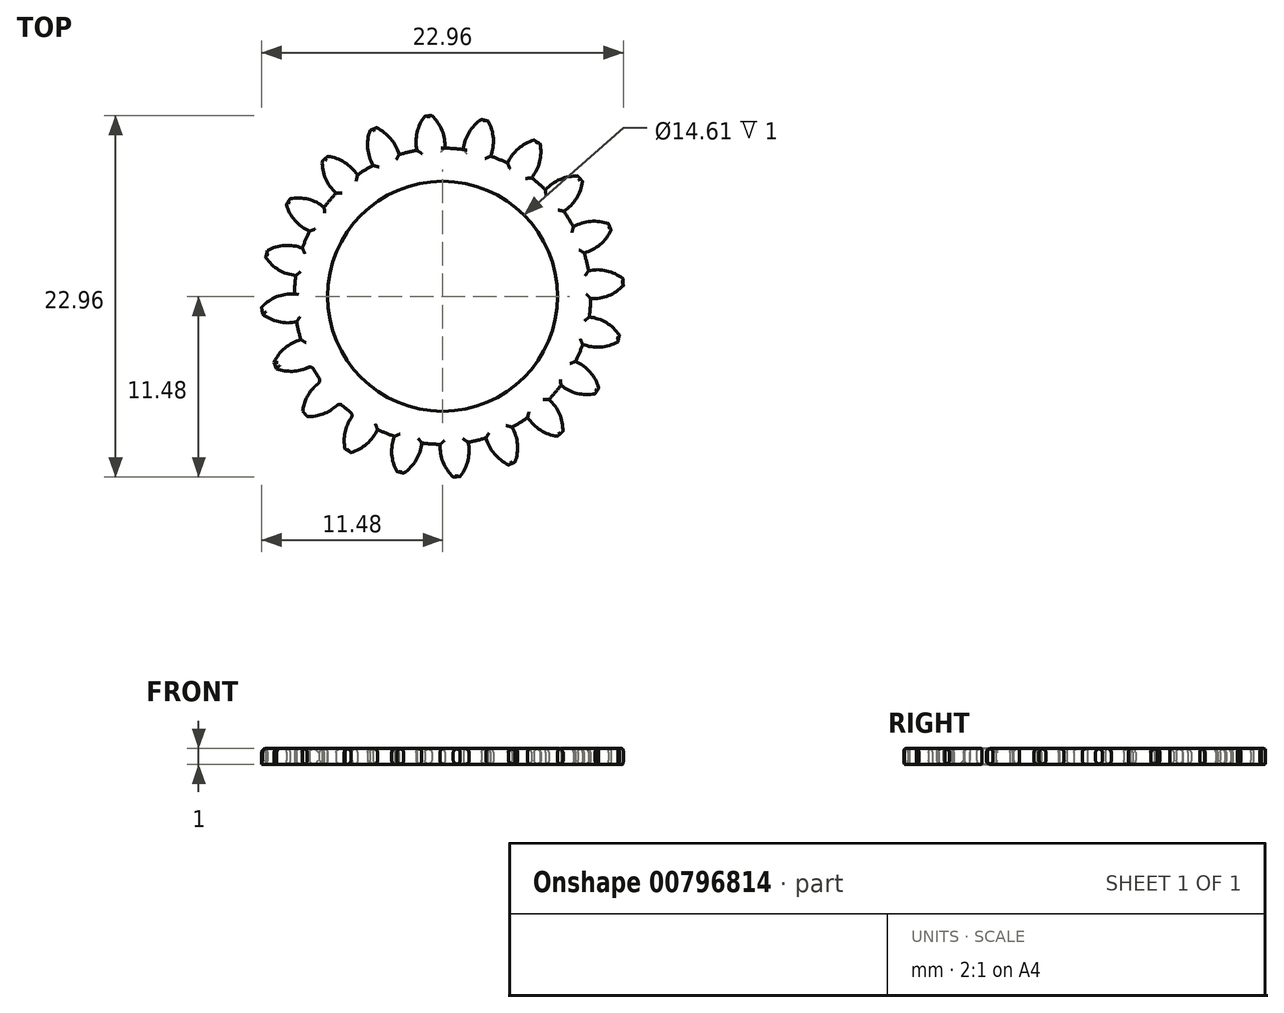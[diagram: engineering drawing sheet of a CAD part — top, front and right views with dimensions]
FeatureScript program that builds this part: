
annotation { "Feature Type Name" : "Feature", "Feature Type Description" : "" }
export const myFeature = defineFeature(function(context is Context, id is Id, definition is map)
    precondition{}
    {
        {
            assignVariable(context, id + "F0", {"name" : "GearDepth", "anyValue" : 1});
        }
        {
            assignVariable(context, id + "F1", {"name" : "TeethFillet", "anyValue" : getVariable(context, 'GearDepth') * .25});
        }
        {
            var Q0;
            Q0=qCreatedBy(makeId("Top.planeOp"),FACE);
            var sketch = newSketch(context, id + "F2", { "sketchPlane" : qUnion([Q0])});
            skCircle(sketch, "E0", {"center": v(0, 0) * mm, "radius": 9.4 * mm});
            skCircle(sketch, "E1", {"center": v(0, 0) * mm, "radius": 10.45 * mm, "construction": true});
            skCircle(sketch, "E2", {"center": v(0, 0) * mm, "radius": 11.5 * mm, "construction": true});
            skLineSegment(sketch, "E3", {"start": v(0, 0) * mm, "end": v(0, 17.6) * mm, "construction": true});
            skLineSegment(sketch, "E4", {"start": v(0, 0) * mm, "end": v(-1.42, 18) * mm, "construction": true});
            skLineSegment(sketch, "E5", {"start": v(0, 10.45) * mm, "end": v(-10.54, 10.45) * mm, "construction": true});
            skLineSegment(sketch, "E6", {"start": v(0, 10.45) * mm, "end": v(-10.3, 6.7) * mm, "construction": true});
            skCircle(sketch, "E7", {"center": v(0, 10.45) * mm, "radius": 2.61 * mm, "construction": true});
            skCircle(sketch, "E8", {"center": v(-2.46, 9.56) * mm, "radius": 2.61 * mm, "construction": true});
            skArc(sketch, "E9", {"start": v(-4.91, 10.45) * mm, "mid": v(-4.92, 10.42) * mm, "end": v(-4.94, 10.39) * mm});
            skArc(sketch, "E10.trimOffspring", {"start": v(0.15, 9.4) * mm, "mid": v(-0.03, 10.54) * mm, "end": v(-0.68, 11.48) * mm});
            skArc(sketch, "E11.MirrorCS", {"start": v(-1.62, 9.27) * mm, "mid": v(-1.62, 10.41) * mm, "end": v(-1.12, 11.45) * mm});
            skLineSegment(sketch, "E12", {"start": v(-1.12, 11.45) * mm, "end": v(-0.68, 11.48) * mm});
            skArc(sketch, "E13.1.0", {"start": v(-2.76, 9) * mm, "mid": v(-3.29, 10.01) * mm, "end": v(-4.2, 10.7) * mm});
            skLineSegment(sketch, "E13.1.1", {"start": v(-4.6, 10.54) * mm, "end": v(-4.2, 10.7) * mm});
            skArc(sketch, "E13.1.2", {"start": v(-4.4, 8.31) * mm, "mid": v(-4.76, 9.4) * mm, "end": v(-4.6, 10.54) * mm});
            skArc(sketch, "E13.2.0", {"start": v(-5.4, 7.7) * mm, "mid": v(-6.22, 8.5) * mm, "end": v(-7.3, 8.89) * mm});
            skLineSegment(sketch, "E13.2.1", {"start": v(-7.64, 8.6) * mm, "end": v(-7.3, 8.89) * mm});
            skArc(sketch, "E13.2.2", {"start": v(-6.76, 6.54) * mm, "mid": v(-7.43, 7.47) * mm, "end": v(-7.64, 8.6) * mm});
            skArc(sketch, "E13.3.0", {"start": v(-7.52, 5.65) * mm, "mid": v(-8.54, 6.17) * mm, "end": v(-9.69, 6.2) * mm});
            skLineSegment(sketch, "E13.3.1", {"start": v(-9.92, 5.82) * mm, "end": v(-9.69, 6.2) * mm});
            skArc(sketch, "E13.3.2", {"start": v(-8.45, 4.13) * mm, "mid": v(-9.37, 4.81) * mm, "end": v(-9.92, 5.82) * mm});
            skArc(sketch, "E13.4.0", {"start": v(-8.9, 3.05) * mm, "mid": v(-10.03, 3.23) * mm, "end": v(-11.13, 2.9) * mm});
            skLineSegment(sketch, "E13.4.1", {"start": v(-11.23, 2.47) * mm, "end": v(-11.13, 2.9) * mm});
            skArc(sketch, "E13.4.2", {"start": v(-9.32, 1.32) * mm, "mid": v(-10.4, 1.68) * mm, "end": v(-11.23, 2.47) * mm});
            skArc(sketch, "E13.5.0", {"start": v(-9.4, 0.15) * mm, "mid": v(-10.54, -0.03) * mm, "end": v(-11.48, -0.68) * mm});
            skLineSegment(sketch, "E13.5.1", {"start": v(-11.45, -1.12) * mm, "end": v(-11.48, -0.68) * mm});
            skArc(sketch, "E13.5.2", {"start": v(-9.27, -1.62) * mm, "mid": v(-10.41, -1.62) * mm, "end": v(-11.45, -1.12) * mm});
            skArc(sketch, "E13.6.0", {"start": v(-9, -2.76) * mm, "mid": v(-10.01, -3.29) * mm, "end": v(-10.7, -4.2) * mm});
            skLineSegment(sketch, "E13.6.1", {"start": v(-10.54, -4.6) * mm, "end": v(-10.7, -4.2) * mm});
            skArc(sketch, "E13.6.2", {"start": v(-8.31, -4.4) * mm, "mid": v(-9.4, -4.76) * mm, "end": v(-10.54, -4.6) * mm});
            skArc(sketch, "E13.7.0", {"start": v(-7.7, -5.4) * mm, "mid": v(-8.5, -6.22) * mm, "end": v(-8.89, -7.3) * mm});
            skLineSegment(sketch, "E13.7.1", {"start": v(-8.6, -7.64) * mm, "end": v(-8.89, -7.3) * mm});
            skArc(sketch, "E13.7.2", {"start": v(-6.54, -6.76) * mm, "mid": v(-7.47, -7.43) * mm, "end": v(-8.6, -7.64) * mm});
            skArc(sketch, "E13.8.0", {"start": v(-5.65, -7.52) * mm, "mid": v(-6.17, -8.54) * mm, "end": v(-6.2, -9.69) * mm});
            skLineSegment(sketch, "E13.8.1", {"start": v(-5.82, -9.92) * mm, "end": v(-6.2, -9.69) * mm});
            skArc(sketch, "E13.8.2", {"start": v(-4.13, -8.45) * mm, "mid": v(-4.81, -9.37) * mm, "end": v(-5.82, -9.92) * mm});
            skArc(sketch, "E13.9.0", {"start": v(-3.05, -8.9) * mm, "mid": v(-3.23, -10.03) * mm, "end": v(-2.9, -11.13) * mm});
            skLineSegment(sketch, "E13.9.1", {"start": v(-2.47, -11.23) * mm, "end": v(-2.9, -11.13) * mm});
            skArc(sketch, "E13.9.2", {"start": v(-1.32, -9.32) * mm, "mid": v(-1.68, -10.4) * mm, "end": v(-2.47, -11.23) * mm});
            skArc(sketch, "E13.10.0", {"start": v(-0.15, -9.4) * mm, "mid": v(0.03, -10.54) * mm, "end": v(0.68, -11.48) * mm});
            skLineSegment(sketch, "E13.10.1", {"start": v(1.12, -11.45) * mm, "end": v(0.68, -11.48) * mm});
            skArc(sketch, "E13.10.2", {"start": v(1.62, -9.27) * mm, "mid": v(1.62, -10.41) * mm, "end": v(1.12, -11.45) * mm});
            skArc(sketch, "E13.11.0", {"start": v(2.76, -9) * mm, "mid": v(3.29, -10.01) * mm, "end": v(4.2, -10.7) * mm});
            skLineSegment(sketch, "E13.11.1", {"start": v(4.6, -10.54) * mm, "end": v(4.2, -10.7) * mm});
            skArc(sketch, "E13.11.2", {"start": v(4.4, -8.31) * mm, "mid": v(4.76, -9.4) * mm, "end": v(4.6, -10.54) * mm});
            skArc(sketch, "E13.12.0", {"start": v(5.4, -7.7) * mm, "mid": v(6.22, -8.5) * mm, "end": v(7.3, -8.89) * mm});
            skLineSegment(sketch, "E13.12.1", {"start": v(7.64, -8.6) * mm, "end": v(7.3, -8.89) * mm});
            skArc(sketch, "E13.12.2", {"start": v(6.76, -6.54) * mm, "mid": v(7.43, -7.47) * mm, "end": v(7.64, -8.6) * mm});
            skArc(sketch, "E13.13.0", {"start": v(7.52, -5.65) * mm, "mid": v(8.54, -6.17) * mm, "end": v(9.69, -6.2) * mm});
            skLineSegment(sketch, "E13.13.1", {"start": v(9.92, -5.82) * mm, "end": v(9.69, -6.2) * mm});
            skArc(sketch, "E13.13.2", {"start": v(8.45, -4.13) * mm, "mid": v(9.37, -4.81) * mm, "end": v(9.92, -5.82) * mm});
            skArc(sketch, "E13.14.0", {"start": v(8.9, -3.05) * mm, "mid": v(10.03, -3.23) * mm, "end": v(11.13, -2.9) * mm});
            skLineSegment(sketch, "E13.14.1", {"start": v(11.23, -2.47) * mm, "end": v(11.13, -2.9) * mm});
            skArc(sketch, "E13.14.2", {"start": v(9.32, -1.32) * mm, "mid": v(10.4, -1.68) * mm, "end": v(11.23, -2.47) * mm});
            skArc(sketch, "E13.15.0", {"start": v(9.4, -0.15) * mm, "mid": v(10.54, 0.03) * mm, "end": v(11.48, 0.68) * mm});
            skLineSegment(sketch, "E13.15.1", {"start": v(11.45, 1.12) * mm, "end": v(11.48, 0.68) * mm});
            skArc(sketch, "E13.15.2", {"start": v(9.27, 1.62) * mm, "mid": v(10.41, 1.62) * mm, "end": v(11.45, 1.12) * mm});
            skArc(sketch, "E13.16.0", {"start": v(9, 2.76) * mm, "mid": v(10.01, 3.29) * mm, "end": v(10.7, 4.2) * mm});
            skLineSegment(sketch, "E13.16.1", {"start": v(10.54, 4.6) * mm, "end": v(10.7, 4.2) * mm});
            skArc(sketch, "E13.16.2", {"start": v(8.31, 4.4) * mm, "mid": v(9.4, 4.76) * mm, "end": v(10.54, 4.6) * mm});
            skArc(sketch, "E13.17.0", {"start": v(7.7, 5.4) * mm, "mid": v(8.5, 6.22) * mm, "end": v(8.89, 7.3) * mm});
            skLineSegment(sketch, "E13.17.1", {"start": v(8.6, 7.64) * mm, "end": v(8.89, 7.3) * mm});
            skArc(sketch, "E13.17.2", {"start": v(6.54, 6.76) * mm, "mid": v(7.47, 7.43) * mm, "end": v(8.6, 7.64) * mm});
            skArc(sketch, "E13.18.0", {"start": v(5.65, 7.52) * mm, "mid": v(6.17, 8.54) * mm, "end": v(6.2, 9.69) * mm});
            skLineSegment(sketch, "E13.18.1", {"start": v(5.82, 9.92) * mm, "end": v(6.2, 9.69) * mm});
            skArc(sketch, "E13.18.2", {"start": v(4.13, 8.45) * mm, "mid": v(4.81, 9.37) * mm, "end": v(5.82, 9.92) * mm});
            skArc(sketch, "E13.19.0", {"start": v(3.05, 8.9) * mm, "mid": v(3.23, 10.03) * mm, "end": v(2.9, 11.13) * mm});
            skLineSegment(sketch, "E13.19.1", {"start": v(2.47, 11.23) * mm, "end": v(2.9, 11.13) * mm});
            skArc(sketch, "E13.19.2", {"start": v(1.32, 9.32) * mm, "mid": v(1.68, 10.4) * mm, "end": v(2.47, 11.23) * mm});
            skCircle(sketch, "E14", {"center": v(0, 0) * mm, "radius": 2.5 * mm});
            skSolve(sketch);
        }
        {
            var Q0;
            {var subQ0=sQuery(id+"F2.wireOp",EDGE,"E10.trimOffspring");Q0=makeQuery(id+"F2.imprint","IMPRINT",FACE,{"disambiguationData":[TD([[makeQuery(id+"F2.imprint","IMPRINT",EDGE,{"derivedFrom":subQ0}),1.0]])]});}
            var Q1;
            {var subQ0=sQuery(id+"F2.wireOp",EDGE,"E0");var subQ1=makeQuery(id+"F2.imprint","INTERSECT",VERTEX,{"derivedFrom":[subQ0,sQuery(id+"F2.wireOp",EDGE,"E10.trimOffspring")]});Q1=makeQuery(id+"F2.imprint","IMPRINT",FACE,{"disambiguationData":[TD([[makeQuery(id+"F2.imprint","IMPRINT",EDGE,{"disambiguationData":[TD([[subQ1,-1.0]])],"derivedFrom":subQ0}),1.0]])]});}
            var Q2;
            {var subQ0=sQuery(id+"F2.wireOp",EDGE,"E13.1.0");Q2=makeQuery(id+"F2.imprint","IMPRINT",FACE,{"disambiguationData":[TD([[makeQuery(id+"F2.imprint","IMPRINT",EDGE,{"derivedFrom":subQ0}),1.0]])]});}
            var Q3;
            {var subQ0=sQuery(id+"F2.wireOp",EDGE,"E13.2.0");Q3=makeQuery(id+"F2.imprint","IMPRINT",FACE,{"disambiguationData":[TD([[makeQuery(id+"F2.imprint","IMPRINT",EDGE,{"derivedFrom":subQ0}),1.0]])]});}
            var Q4;
            {var subQ0=sQuery(id+"F2.wireOp",EDGE,"E13.3.0");Q4=makeQuery(id+"F2.imprint","IMPRINT",FACE,{"disambiguationData":[TD([[makeQuery(id+"F2.imprint","IMPRINT",EDGE,{"derivedFrom":subQ0}),1.0]])]});}
            var Q5;
            {var subQ0=sQuery(id+"F2.wireOp",EDGE,"E13.4.0");Q5=makeQuery(id+"F2.imprint","IMPRINT",FACE,{"disambiguationData":[TD([[makeQuery(id+"F2.imprint","IMPRINT",EDGE,{"derivedFrom":subQ0}),1.0]])]});}
            var Q6;
            {var subQ0=sQuery(id+"F2.wireOp",EDGE,"E13.5.0");Q6=makeQuery(id+"F2.imprint","IMPRINT",FACE,{"disambiguationData":[TD([[makeQuery(id+"F2.imprint","IMPRINT",EDGE,{"derivedFrom":subQ0}),1.0]])]});}
            var Q7;
            {var subQ0=sQuery(id+"F2.wireOp",EDGE,"E13.6.0");Q7=makeQuery(id+"F2.imprint","IMPRINT",FACE,{"disambiguationData":[TD([[makeQuery(id+"F2.imprint","IMPRINT",EDGE,{"derivedFrom":subQ0}),1.0]])]});}
            var Q8;
            {var subQ0=sQuery(id+"F2.wireOp",EDGE,"E13.7.0");Q8=makeQuery(id+"F2.imprint","IMPRINT",FACE,{"disambiguationData":[TD([[makeQuery(id+"F2.imprint","IMPRINT",EDGE,{"derivedFrom":subQ0}),1.0]])]});}
            var Q9;
            {var subQ0=sQuery(id+"F2.wireOp",EDGE,"E13.8.0");Q9=makeQuery(id+"F2.imprint","IMPRINT",FACE,{"disambiguationData":[TD([[makeQuery(id+"F2.imprint","IMPRINT",EDGE,{"derivedFrom":subQ0}),1.0]])]});}
            var Q10;
            {var subQ0=sQuery(id+"F2.wireOp",EDGE,"E13.9.0");Q10=makeQuery(id+"F2.imprint","IMPRINT",FACE,{"disambiguationData":[TD([[makeQuery(id+"F2.imprint","IMPRINT",EDGE,{"derivedFrom":subQ0}),1.0]])]});}
            var Q11;
            {var subQ0=sQuery(id+"F2.wireOp",EDGE,"E13.10.0");Q11=makeQuery(id+"F2.imprint","IMPRINT",FACE,{"disambiguationData":[TD([[makeQuery(id+"F2.imprint","IMPRINT",EDGE,{"derivedFrom":subQ0}),1.0]])]});}
            var Q12;
            {var subQ0=sQuery(id+"F2.wireOp",EDGE,"E13.11.0");Q12=makeQuery(id+"F2.imprint","IMPRINT",FACE,{"disambiguationData":[TD([[makeQuery(id+"F2.imprint","IMPRINT",EDGE,{"derivedFrom":subQ0}),1.0]])]});}
            var Q13;
            {var subQ0=sQuery(id+"F2.wireOp",EDGE,"E13.12.0");Q13=makeQuery(id+"F2.imprint","IMPRINT",FACE,{"disambiguationData":[TD([[makeQuery(id+"F2.imprint","IMPRINT",EDGE,{"derivedFrom":subQ0}),1.0]])]});}
            var Q14;
            {var subQ0=sQuery(id+"F2.wireOp",EDGE,"E13.13.0");Q14=makeQuery(id+"F2.imprint","IMPRINT",FACE,{"disambiguationData":[TD([[makeQuery(id+"F2.imprint","IMPRINT",EDGE,{"derivedFrom":subQ0}),1.0]])]});}
            var Q15;
            {var subQ0=sQuery(id+"F2.wireOp",EDGE,"E13.14.0");Q15=makeQuery(id+"F2.imprint","IMPRINT",FACE,{"disambiguationData":[TD([[makeQuery(id+"F2.imprint","IMPRINT",EDGE,{"derivedFrom":subQ0}),1.0]])]});}
            var Q16;
            {var subQ0=sQuery(id+"F2.wireOp",EDGE,"E13.15.0");Q16=makeQuery(id+"F2.imprint","IMPRINT",FACE,{"disambiguationData":[TD([[makeQuery(id+"F2.imprint","IMPRINT",EDGE,{"derivedFrom":subQ0}),1.0]])]});}
            var Q17;
            {var subQ0=sQuery(id+"F2.wireOp",EDGE,"E13.16.0");Q17=makeQuery(id+"F2.imprint","IMPRINT",FACE,{"disambiguationData":[TD([[makeQuery(id+"F2.imprint","IMPRINT",EDGE,{"derivedFrom":subQ0}),1.0]])]});}
            var Q18;
            {var subQ0=sQuery(id+"F2.wireOp",EDGE,"E13.17.0");Q18=makeQuery(id+"F2.imprint","IMPRINT",FACE,{"disambiguationData":[TD([[makeQuery(id+"F2.imprint","IMPRINT",EDGE,{"derivedFrom":subQ0}),1.0]])]});}
            var Q19;
            {var subQ0=sQuery(id+"F2.wireOp",EDGE,"E13.18.0");Q19=makeQuery(id+"F2.imprint","IMPRINT",FACE,{"disambiguationData":[TD([[makeQuery(id+"F2.imprint","IMPRINT",EDGE,{"derivedFrom":subQ0}),1.0]])]});}
            var Q20;
            {var subQ0=sQuery(id+"F2.wireOp",EDGE,"E13.19.0");Q20=makeQuery(id+"F2.imprint","IMPRINT",FACE,{"disambiguationData":[TD([[makeQuery(id+"F2.imprint","IMPRINT",EDGE,{"derivedFrom":subQ0}),1.0]])]});}
            var Q21;
            Q21=sQuery(id+"F2.wireOp",EDGE,"E0");
            var Q22;
            Q22=sQuery(id+"F2.wireOp",EDGE,"E10.trimOffspring");
            var Q23;
            Q23=sQuery(id+"F2.wireOp",EDGE,"E12");
            var Q24;
            Q24=sQuery(id+"F2.wireOp",EDGE,"E11.MirrorCS");
            extrude(context, id + "F3", {"entities" : qUnion([Q0, Q1, Q2, Q3, Q4, Q5, Q6, Q7, Q8, Q9, Q10, Q11, Q12, Q13, Q14, Q15, Q16, Q17, Q18, Q19, Q20]), "surfaceEntities" : qUnion([Q21, Q22, Q23, Q24]), "depth" : (getVariable(context, 'GearDepth')) * mm});
        }
        {
            var Q0;
            Q0=makeQuery(id+"F3.opExtrude","CAP_EDGE",EDGE,{"disambiguationData":[OSD([sQuery(id+"F2.wireOp",EDGE,"E13.5.2")])],"isStart":false});
            var Q1;
            Q1=makeQuery(id+"F3.opExtrude","CAP_EDGE",EDGE,{"disambiguationData":[OSD([sQuery(id+"F2.wireOp",EDGE,"E13.5.1")])],"isStart":false});
            var Q2;
            {var subQ0=sQuery(id+"F2.wireOp",EDGE,"E0");Q2=makeQuery(id+"F3.opExtrude","CAP_EDGE",EDGE,{"disambiguationData":[OSD([subQ0]),TDD([makeQuery(id+"F2.imprint","IMPRINT",EDGE,{"disambiguationData":[TD([[makeQuery(id+"F2.imprint","INTERSECT",VERTEX,{"derivedFrom":[subQ0,sQuery(id+"F2.wireOp",EDGE,"E13.5.2")]}),-1.0]])],"derivedFrom":subQ0})])],"isStart":false});}
            var Q3;
            Q3=makeQuery(id+"F3.opExtrude","CAP_EDGE",EDGE,{"disambiguationData":[OSD([sQuery(id+"F2.wireOp",EDGE,"E13.6.0")])],"isStart":false});
            var Q4;
            Q4=makeQuery(id+"F3.opExtrude","CAP_EDGE",EDGE,{"disambiguationData":[OSD([sQuery(id+"F2.wireOp",EDGE,"E13.6.1")])],"isStart":false});
            var Q5;
            Q5=makeQuery(id+"F3.opExtrude","CAP_EDGE",EDGE,{"disambiguationData":[OSD([sQuery(id+"F2.wireOp",EDGE,"E13.6.2")])],"isStart":false});
            var Q6;
            {var subQ0=sQuery(id+"F2.wireOp",EDGE,"E0");Q6=makeQuery(id+"F3.opExtrude","SWEPT_FACE",FACE,{"disambiguationData":[OSD([subQ0]),TDD([makeQuery(id+"F2.imprint","IMPRINT",EDGE,{"disambiguationData":[TD([[makeQuery(id+"F2.imprint","INTERSECT",VERTEX,{"derivedFrom":[subQ0,sQuery(id+"F2.wireOp",EDGE,"E13.6.2")]}),-1.0]])],"derivedFrom":subQ0})])]});}
            var Q7;
            {var subQ0=sQuery(id+"F2.wireOp",EDGE,"E0");Q7=makeQuery(id+"F3.opExtrude","CAP_EDGE",EDGE,{"disambiguationData":[OSD([subQ0]),TDD([makeQuery(id+"F2.imprint","IMPRINT",EDGE,{"disambiguationData":[TD([[makeQuery(id+"F2.imprint","INTERSECT",VERTEX,{"derivedFrom":[subQ0,sQuery(id+"F2.wireOp",EDGE,"E13.6.2")]}),-1.0]])],"derivedFrom":subQ0})])],"isStart":false});}
            var Q8;
            Q8=makeQuery(id+"F3.opExtrude","CAP_EDGE",EDGE,{"disambiguationData":[OSD([sQuery(id+"F2.wireOp",EDGE,"E13.7.2")])],"isStart":true});
            var Q9;
            {var subQ0=sQuery(id+"F2.wireOp",EDGE,"E0");Q9=makeQuery(id+"F3.opExtrude","CAP_EDGE",EDGE,{"disambiguationData":[OSD([subQ0]),TDD([makeQuery(id+"F2.imprint","IMPRINT",EDGE,{"disambiguationData":[TD([[makeQuery(id+"F2.imprint","INTERSECT",VERTEX,{"derivedFrom":[subQ0,sQuery(id+"F2.wireOp",EDGE,"E13.7.2")]}),-1.0]])],"derivedFrom":subQ0})])],"isStart":true});}
            var Q10;
            Q10=makeQuery(id+"F3.opExtrude","CAP_EDGE",EDGE,{"disambiguationData":[OSD([sQuery(id+"F2.wireOp",EDGE,"E13.7.2")])],"isStart":false});
            var Q11;
            {var subQ0=sQuery(id+"F2.wireOp",EDGE,"E0");Q11=makeQuery(id+"F3.opExtrude","CAP_EDGE",EDGE,{"disambiguationData":[OSD([subQ0]),TDD([makeQuery(id+"F2.imprint","IMPRINT",EDGE,{"disambiguationData":[TD([[makeQuery(id+"F2.imprint","INTERSECT",VERTEX,{"derivedFrom":[subQ0,sQuery(id+"F2.wireOp",EDGE,"E13.7.2")]}),-1.0]])],"derivedFrom":subQ0})])],"isStart":false});}
            var Q12;
            Q12=makeQuery(id+"F3.opExtrude","CAP_EDGE",EDGE,{"disambiguationData":[OSD([sQuery(id+"F2.wireOp",EDGE,"E13.8.0")])],"isStart":false});
            var Q13;
            {var subQ0=sQuery(id+"F2.wireOp",EDGE,"E0");Q13=makeQuery(id+"F3.opExtrude","SWEPT_FACE",FACE,{"disambiguationData":[OSD([subQ0]),TDD([makeQuery(id+"F2.imprint","IMPRINT",EDGE,{"disambiguationData":[TD([[makeQuery(id+"F2.imprint","INTERSECT",VERTEX,{"derivedFrom":[subQ0,sQuery(id+"F2.wireOp",EDGE,"E13.7.2")]}),-1.0]])],"derivedFrom":subQ0})])]});}
            var Q14;
            Q14=makeQuery(id+"F3.opExtrude","CAP_EDGE",EDGE,{"disambiguationData":[OSD([sQuery(id+"F2.wireOp",EDGE,"E13.6.0")])],"isStart":true});
            var Q15;
            Q15=makeQuery(id+"F3.opExtrude","CAP_EDGE",EDGE,{"disambiguationData":[OSD([sQuery(id+"F2.wireOp",EDGE,"E13.8.2")])],"isStart":false});
            var Q16;
            {var subQ0=sQuery(id+"F2.wireOp",EDGE,"E0");Q16=makeQuery(id+"F3.opExtrude","CAP_EDGE",EDGE,{"disambiguationData":[OSD([subQ0]),TDD([makeQuery(id+"F2.imprint","IMPRINT",EDGE,{"disambiguationData":[TD([[makeQuery(id+"F2.imprint","INTERSECT",VERTEX,{"derivedFrom":[subQ0,sQuery(id+"F2.wireOp",EDGE,"E13.8.2")]}),-1.0]])],"derivedFrom":subQ0})])],"isStart":false});}
            var Q17;
            Q17=makeQuery(id+"F3.opExtrude","CAP_EDGE",EDGE,{"disambiguationData":[OSD([sQuery(id+"F2.wireOp",EDGE,"E13.9.0")])],"isStart":false});
            var Q18;
            Q18=makeQuery(id+"F3.opExtrude","CAP_EDGE",EDGE,{"disambiguationData":[OSD([sQuery(id+"F2.wireOp",EDGE,"E13.9.2")])],"isStart":false});
            var Q19;
            {var subQ0=sQuery(id+"F2.wireOp",EDGE,"E0");Q19=makeQuery(id+"F3.opExtrude","CAP_EDGE",EDGE,{"disambiguationData":[OSD([subQ0]),TDD([makeQuery(id+"F2.imprint","IMPRINT",EDGE,{"disambiguationData":[TD([[makeQuery(id+"F2.imprint","INTERSECT",VERTEX,{"derivedFrom":[subQ0,sQuery(id+"F2.wireOp",EDGE,"E13.9.2")]}),-1.0]])],"derivedFrom":subQ0})])],"isStart":false});}
            var Q20;
            Q20=makeQuery(id+"F3.opExtrude","CAP_EDGE",EDGE,{"disambiguationData":[OSD([sQuery(id+"F2.wireOp",EDGE,"E13.10.0")])],"isStart":false});
            var Q21;
            Q21=makeQuery(id+"F3.opExtrude","CAP_EDGE",EDGE,{"disambiguationData":[OSD([sQuery(id+"F2.wireOp",EDGE,"E13.10.2")])],"isStart":false});
            var Q22;
            {var subQ0=sQuery(id+"F2.wireOp",EDGE,"E0");Q22=makeQuery(id+"F3.opExtrude","CAP_EDGE",EDGE,{"disambiguationData":[OSD([subQ0]),TDD([makeQuery(id+"F2.imprint","IMPRINT",EDGE,{"disambiguationData":[TD([[makeQuery(id+"F2.imprint","INTERSECT",VERTEX,{"derivedFrom":[subQ0,sQuery(id+"F2.wireOp",EDGE,"E13.10.2")]}),-1.0]])],"derivedFrom":subQ0})])],"isStart":false});}
            var Q23;
            Q23=makeQuery(id+"F3.opExtrude","CAP_EDGE",EDGE,{"disambiguationData":[OSD([sQuery(id+"F2.wireOp",EDGE,"E13.11.0")])],"isStart":false});
            var Q24;
            Q24=makeQuery(id+"F3.opExtrude","CAP_EDGE",EDGE,{"disambiguationData":[OSD([sQuery(id+"F2.wireOp",EDGE,"E13.11.2")])],"isStart":false});
            var Q25;
            {var subQ0=sQuery(id+"F2.wireOp",EDGE,"E0");Q25=makeQuery(id+"F3.opExtrude","CAP_EDGE",EDGE,{"disambiguationData":[OSD([subQ0]),TDD([makeQuery(id+"F2.imprint","IMPRINT",EDGE,{"disambiguationData":[TD([[makeQuery(id+"F2.imprint","INTERSECT",VERTEX,{"derivedFrom":[subQ0,sQuery(id+"F2.wireOp",EDGE,"E13.11.2")]}),-1.0]])],"derivedFrom":subQ0})])],"isStart":false});}
            var Q26;
            Q26=makeQuery(id+"F3.opExtrude","CAP_EDGE",EDGE,{"disambiguationData":[OSD([sQuery(id+"F2.wireOp",EDGE,"E13.12.0")])],"isStart":false});
            var Q27;
            Q27=makeQuery(id+"F3.opExtrude","CAP_EDGE",EDGE,{"disambiguationData":[OSD([sQuery(id+"F2.wireOp",EDGE,"E13.12.2")])],"isStart":false});
            var Q28;
            {var subQ0=sQuery(id+"F2.wireOp",EDGE,"E0");Q28=makeQuery(id+"F3.opExtrude","CAP_EDGE",EDGE,{"disambiguationData":[OSD([subQ0]),TDD([makeQuery(id+"F2.imprint","IMPRINT",EDGE,{"disambiguationData":[TD([[makeQuery(id+"F2.imprint","INTERSECT",VERTEX,{"derivedFrom":[subQ0,sQuery(id+"F2.wireOp",EDGE,"E13.12.2")]}),-1.0]])],"derivedFrom":subQ0})])],"isStart":false});}
            var Q29;
            Q29=makeQuery(id+"F3.opExtrude","CAP_EDGE",EDGE,{"disambiguationData":[OSD([sQuery(id+"F2.wireOp",EDGE,"E13.13.0")])],"isStart":false});
            var Q30;
            Q30=makeQuery(id+"F3.opExtrude","CAP_EDGE",EDGE,{"disambiguationData":[OSD([sQuery(id+"F2.wireOp",EDGE,"E13.13.2")])],"isStart":false});
            var Q31;
            {var subQ0=sQuery(id+"F2.wireOp",EDGE,"E0");Q31=makeQuery(id+"F3.opExtrude","CAP_EDGE",EDGE,{"disambiguationData":[OSD([subQ0]),TDD([makeQuery(id+"F2.imprint","IMPRINT",EDGE,{"disambiguationData":[TD([[makeQuery(id+"F2.imprint","INTERSECT",VERTEX,{"derivedFrom":[subQ0,sQuery(id+"F2.wireOp",EDGE,"E13.13.2")]}),-1.0]])],"derivedFrom":subQ0})])],"isStart":false});}
            var Q32;
            Q32=makeQuery(id+"F3.opExtrude","CAP_EDGE",EDGE,{"disambiguationData":[OSD([sQuery(id+"F2.wireOp",EDGE,"E13.14.0")])],"isStart":false});
            var Q33;
            Q33=makeQuery(id+"F3.opExtrude","CAP_EDGE",EDGE,{"disambiguationData":[OSD([sQuery(id+"F2.wireOp",EDGE,"E13.14.2")])],"isStart":false});
            var Q34;
            {var subQ0=sQuery(id+"F2.wireOp",EDGE,"E0");Q34=makeQuery(id+"F3.opExtrude","CAP_EDGE",EDGE,{"disambiguationData":[OSD([subQ0]),TDD([makeQuery(id+"F2.imprint","IMPRINT",EDGE,{"disambiguationData":[TD([[makeQuery(id+"F2.imprint","INTERSECT",VERTEX,{"derivedFrom":[subQ0,sQuery(id+"F2.wireOp",EDGE,"E13.14.2")]}),-1.0]])],"derivedFrom":subQ0})])],"isStart":false});}
            var Q35;
            Q35=makeQuery(id+"F3.opExtrude","CAP_EDGE",EDGE,{"disambiguationData":[OSD([sQuery(id+"F2.wireOp",EDGE,"E13.15.0")])],"isStart":false});
            var Q36;
            {var subQ0=sQuery(id+"F2.wireOp",EDGE,"E0");Q36=makeQuery(id+"F3.opExtrude","CAP_EDGE",EDGE,{"disambiguationData":[OSD([subQ0]),TDD([makeQuery(id+"F2.imprint","IMPRINT",EDGE,{"disambiguationData":[TD([[makeQuery(id+"F2.imprint","INTERSECT",VERTEX,{"derivedFrom":[subQ0,sQuery(id+"F2.wireOp",EDGE,"E13.14.2")]}),-1.0]])],"derivedFrom":subQ0})])],"isStart":false});}
            var Q37;
            Q37=makeQuery(id+"F3.opExtrude","CAP_EDGE",EDGE,{"disambiguationData":[OSD([sQuery(id+"F2.wireOp",EDGE,"E13.15.2")])],"isStart":false});
            var Q38;
            {var subQ0=sQuery(id+"F2.wireOp",EDGE,"E0");Q38=makeQuery(id+"F3.opExtrude","CAP_EDGE",EDGE,{"disambiguationData":[OSD([subQ0]),TDD([makeQuery(id+"F2.imprint","IMPRINT",EDGE,{"disambiguationData":[TD([[makeQuery(id+"F2.imprint","INTERSECT",VERTEX,{"derivedFrom":[subQ0,sQuery(id+"F2.wireOp",EDGE,"E13.15.2")]}),-1.0]])],"derivedFrom":subQ0})])],"isStart":false});}
            var Q39;
            Q39=makeQuery(id+"F3.opExtrude","CAP_EDGE",EDGE,{"disambiguationData":[OSD([sQuery(id+"F2.wireOp",EDGE,"E13.16.0")])],"isStart":false});
            var Q40;
            Q40=makeQuery(id+"F3.opExtrude","CAP_EDGE",EDGE,{"disambiguationData":[OSD([sQuery(id+"F2.wireOp",EDGE,"E13.16.2")])],"isStart":false});
            var Q41;
            Q41=makeQuery(id+"F3.opExtrude","CAP_EDGE",EDGE,{"disambiguationData":[OSD([sQuery(id+"F2.wireOp",EDGE,"E13.17.0")])],"isStart":false});
            var Q42;
            {var subQ0=sQuery(id+"F2.wireOp",EDGE,"E0");Q42=makeQuery(id+"F3.opExtrude","CAP_EDGE",EDGE,{"disambiguationData":[OSD([subQ0]),TDD([makeQuery(id+"F2.imprint","IMPRINT",EDGE,{"disambiguationData":[TD([[makeQuery(id+"F2.imprint","INTERSECT",VERTEX,{"derivedFrom":[subQ0,sQuery(id+"F2.wireOp",EDGE,"E13.16.2")]}),-1.0]])],"derivedFrom":subQ0})])],"isStart":false});}
            var Q43;
            Q43=makeQuery(id+"F3.opExtrude","CAP_EDGE",EDGE,{"disambiguationData":[OSD([sQuery(id+"F2.wireOp",EDGE,"E13.17.2")])],"isStart":false});
            var Q44;
            {var subQ0=sQuery(id+"F2.wireOp",EDGE,"E0");Q44=makeQuery(id+"F3.opExtrude","CAP_EDGE",EDGE,{"disambiguationData":[OSD([subQ0]),TDD([makeQuery(id+"F2.imprint","IMPRINT",EDGE,{"disambiguationData":[TD([[makeQuery(id+"F2.imprint","INTERSECT",VERTEX,{"derivedFrom":[subQ0,sQuery(id+"F2.wireOp",EDGE,"E13.17.2")]}),-1.0]])],"derivedFrom":subQ0})])],"isStart":false});}
            var Q45;
            Q45=makeQuery(id+"F3.opExtrude","CAP_EDGE",EDGE,{"disambiguationData":[OSD([sQuery(id+"F2.wireOp",EDGE,"E13.18.0")])],"isStart":false});
            var Q46;
            Q46=makeQuery(id+"F3.opExtrude","CAP_EDGE",EDGE,{"disambiguationData":[OSD([sQuery(id+"F2.wireOp",EDGE,"E13.18.2")])],"isStart":false});
            var Q47;
            {var subQ0=sQuery(id+"F2.wireOp",EDGE,"E0");Q47=makeQuery(id+"F3.opExtrude","CAP_EDGE",EDGE,{"disambiguationData":[OSD([subQ0]),TDD([makeQuery(id+"F2.imprint","IMPRINT",EDGE,{"disambiguationData":[TD([[makeQuery(id+"F2.imprint","INTERSECT",VERTEX,{"derivedFrom":[subQ0,sQuery(id+"F2.wireOp",EDGE,"E13.18.2")]}),-1.0]])],"derivedFrom":subQ0})])],"isStart":false});}
            var Q48;
            Q48=makeQuery(id+"F3.opExtrude","CAP_EDGE",EDGE,{"disambiguationData":[OSD([sQuery(id+"F2.wireOp",EDGE,"E13.19.0")])],"isStart":false});
            var Q49;
            Q49=makeQuery(id+"F3.opExtrude","CAP_EDGE",EDGE,{"disambiguationData":[OSD([sQuery(id+"F2.wireOp",EDGE,"E13.19.2")])],"isStart":false});
            var Q50;
            Q50=makeQuery(id+"F3.opExtrude","CAP_EDGE",EDGE,{"disambiguationData":[OSD([sQuery(id+"F2.wireOp",EDGE,"E10.trimOffspring")])],"isStart":false});
            var Q51;
            Q51=makeQuery(id+"F3.opExtrude","CAP_EDGE",EDGE,{"disambiguationData":[OSD([sQuery(id+"F2.wireOp",EDGE,"E11.MirrorCS")])],"isStart":false});
            var Q52;
            {var subQ0=sQuery(id+"F2.wireOp",EDGE,"E0");Q52=makeQuery(id+"F3.opExtrude","CAP_EDGE",EDGE,{"disambiguationData":[OSD([subQ0]),TDD([makeQuery(id+"F2.imprint","IMPRINT",EDGE,{"disambiguationData":[TD([[makeQuery(id+"F2.imprint","INTERSECT",VERTEX,{"derivedFrom":[subQ0,sQuery(id+"F2.wireOp",EDGE,"E11.MirrorCS")]}),-1.0]])],"derivedFrom":subQ0})])],"isStart":false});}
            var Q53;
            Q53=makeQuery(id+"F3.opExtrude","CAP_EDGE",EDGE,{"disambiguationData":[OSD([sQuery(id+"F2.wireOp",EDGE,"E13.1.0")])],"isStart":false});
            var Q54;
            Q54=makeQuery(id+"F3.opExtrude","CAP_EDGE",EDGE,{"disambiguationData":[OSD([sQuery(id+"F2.wireOp",EDGE,"E13.1.2")])],"isStart":false});
            var Q55;
            {var subQ0=sQuery(id+"F2.wireOp",EDGE,"E0");Q55=makeQuery(id+"F3.opExtrude","CAP_EDGE",EDGE,{"disambiguationData":[OSD([subQ0]),TDD([makeQuery(id+"F2.imprint","IMPRINT",EDGE,{"disambiguationData":[TD([[makeQuery(id+"F2.imprint","INTERSECT",VERTEX,{"derivedFrom":[subQ0,sQuery(id+"F2.wireOp",EDGE,"E13.1.2")]}),-1.0]])],"derivedFrom":subQ0})])],"isStart":false});}
            var Q56;
            Q56=makeQuery(id+"F3.opExtrude","CAP_EDGE",EDGE,{"disambiguationData":[OSD([sQuery(id+"F2.wireOp",EDGE,"E13.2.0")])],"isStart":false});
            var Q57;
            Q57=makeQuery(id+"F3.opExtrude","CAP_EDGE",EDGE,{"disambiguationData":[OSD([sQuery(id+"F2.wireOp",EDGE,"E13.2.2")])],"isStart":false});
            var Q58;
            {var subQ0=sQuery(id+"F2.wireOp",EDGE,"E0");Q58=makeQuery(id+"F3.opExtrude","CAP_EDGE",EDGE,{"disambiguationData":[OSD([subQ0]),TDD([makeQuery(id+"F2.imprint","IMPRINT",EDGE,{"disambiguationData":[TD([[makeQuery(id+"F2.imprint","INTERSECT",VERTEX,{"derivedFrom":[subQ0,sQuery(id+"F2.wireOp",EDGE,"E13.2.2")]}),-1.0]])],"derivedFrom":subQ0})])],"isStart":false});}
            var Q59;
            Q59=makeQuery(id+"F3.opExtrude","CAP_EDGE",EDGE,{"disambiguationData":[OSD([sQuery(id+"F2.wireOp",EDGE,"E13.3.0")])],"isStart":false});
            var Q60;
            Q60=makeQuery(id+"F3.opExtrude","CAP_EDGE",EDGE,{"disambiguationData":[OSD([sQuery(id+"F2.wireOp",EDGE,"E13.3.2")])],"isStart":false});
            var Q61;
            {var subQ0=sQuery(id+"F2.wireOp",EDGE,"E0");Q61=makeQuery(id+"F3.opExtrude","CAP_EDGE",EDGE,{"disambiguationData":[OSD([subQ0]),TDD([makeQuery(id+"F2.imprint","IMPRINT",EDGE,{"disambiguationData":[TD([[makeQuery(id+"F2.imprint","INTERSECT",VERTEX,{"derivedFrom":[subQ0,sQuery(id+"F2.wireOp",EDGE,"E13.3.2")]}),-1.0]])],"derivedFrom":subQ0})])],"isStart":false});}
            var Q62;
            Q62=makeQuery(id+"F3.opExtrude","CAP_EDGE",EDGE,{"disambiguationData":[OSD([sQuery(id+"F2.wireOp",EDGE,"E13.4.0")])],"isStart":false});
            var Q63;
            Q63=makeQuery(id+"F3.opExtrude","CAP_EDGE",EDGE,{"disambiguationData":[OSD([sQuery(id+"F2.wireOp",EDGE,"E13.4.2")])],"isStart":false});
            var Q64;
            {var subQ0=sQuery(id+"F2.wireOp",EDGE,"E0");Q64=makeQuery(id+"F3.opExtrude","CAP_EDGE",EDGE,{"disambiguationData":[OSD([subQ0]),TDD([makeQuery(id+"F2.imprint","IMPRINT",EDGE,{"disambiguationData":[TD([[makeQuery(id+"F2.imprint","INTERSECT",VERTEX,{"derivedFrom":[subQ0,sQuery(id+"F2.wireOp",EDGE,"E13.4.2")]}),-1.0]])],"derivedFrom":subQ0})])],"isStart":false});}
            var Q65;
            {var subQ0=sQuery(id+"F2.wireOp",EDGE,"E0");Q65=makeQuery(id+"F3.opExtrude","CAP_EDGE",EDGE,{"disambiguationData":[OSD([subQ0]),TDD([makeQuery(id+"F2.imprint","IMPRINT",EDGE,{"disambiguationData":[TD([[makeQuery(id+"F2.imprint","INTERSECT",VERTEX,{"derivedFrom":[subQ0,sQuery(id+"F2.wireOp",EDGE,"E13.5.2")]}),-1.0]])],"derivedFrom":subQ0})])],"isStart":true});}
            var Q66;
            Q66=makeQuery(id+"F3.opExtrude","CAP_EDGE",EDGE,{"disambiguationData":[OSD([sQuery(id+"F2.wireOp",EDGE,"E13.5.2")])],"isStart":true});
            var Q67;
            {var subQ0=sQuery(id+"F2.wireOp",EDGE,"E0");Q67=makeQuery(id+"F3.opExtrude","CAP_EDGE",EDGE,{"disambiguationData":[OSD([subQ0]),TDD([makeQuery(id+"F2.imprint","IMPRINT",EDGE,{"disambiguationData":[TD([[makeQuery(id+"F2.imprint","INTERSECT",VERTEX,{"derivedFrom":[subQ0,sQuery(id+"F2.wireOp",EDGE,"E13.4.2")]}),-1.0]])],"derivedFrom":subQ0})])],"isStart":true});}
            var Q68;
            Q68=makeQuery(id+"F3.opExtrude","CAP_EDGE",EDGE,{"disambiguationData":[OSD([sQuery(id+"F2.wireOp",EDGE,"E13.4.2")])],"isStart":true});
            var Q69;
            Q69=makeQuery(id+"F3.opExtrude","CAP_EDGE",EDGE,{"disambiguationData":[OSD([sQuery(id+"F2.wireOp",EDGE,"E13.4.0")])],"isStart":true});
            var Q70;
            {var subQ0=sQuery(id+"F2.wireOp",EDGE,"E0");Q70=makeQuery(id+"F3.opExtrude","CAP_EDGE",EDGE,{"disambiguationData":[OSD([subQ0]),TDD([makeQuery(id+"F2.imprint","IMPRINT",EDGE,{"disambiguationData":[TD([[makeQuery(id+"F2.imprint","INTERSECT",VERTEX,{"derivedFrom":[subQ0,sQuery(id+"F2.wireOp",EDGE,"E13.3.2")]}),-1.0]])],"derivedFrom":subQ0})])],"isStart":true});}
            var Q71;
            Q71=makeQuery(id+"F3.opExtrude","CAP_EDGE",EDGE,{"disambiguationData":[OSD([sQuery(id+"F2.wireOp",EDGE,"E13.3.2")])],"isStart":true});
            var Q72;
            Q72=makeQuery(id+"F3.opExtrude","CAP_EDGE",EDGE,{"disambiguationData":[OSD([sQuery(id+"F2.wireOp",EDGE,"E13.3.0")])],"isStart":true});
            var Q73;
            {var subQ0=sQuery(id+"F2.wireOp",EDGE,"E0");Q73=makeQuery(id+"F3.opExtrude","CAP_EDGE",EDGE,{"disambiguationData":[OSD([subQ0]),TDD([makeQuery(id+"F2.imprint","IMPRINT",EDGE,{"disambiguationData":[TD([[makeQuery(id+"F2.imprint","INTERSECT",VERTEX,{"derivedFrom":[subQ0,sQuery(id+"F2.wireOp",EDGE,"E13.2.2")]}),-1.0]])],"derivedFrom":subQ0})])],"isStart":true});}
            var Q74;
            Q74=makeQuery(id+"F3.opExtrude","CAP_EDGE",EDGE,{"disambiguationData":[OSD([sQuery(id+"F2.wireOp",EDGE,"E13.2.2")])],"isStart":true});
            var Q75;
            Q75=makeQuery(id+"F3.opExtrude","CAP_EDGE",EDGE,{"disambiguationData":[OSD([sQuery(id+"F2.wireOp",EDGE,"E13.2.0")])],"isStart":true});
            var Q76;
            Q76=makeQuery(id+"F3.opExtrude","CAP_EDGE",EDGE,{"disambiguationData":[OSD([sQuery(id+"F2.wireOp",EDGE,"E13.1.2")])],"isStart":true});
            var Q77;
            {var subQ0=sQuery(id+"F2.wireOp",EDGE,"E0");Q77=makeQuery(id+"F3.opExtrude","CAP_EDGE",EDGE,{"disambiguationData":[OSD([subQ0]),TDD([makeQuery(id+"F2.imprint","IMPRINT",EDGE,{"disambiguationData":[TD([[makeQuery(id+"F2.imprint","INTERSECT",VERTEX,{"derivedFrom":[subQ0,sQuery(id+"F2.wireOp",EDGE,"E13.1.2")]}),-1.0]])],"derivedFrom":subQ0})])],"isStart":true});}
            var Q78;
            Q78=makeQuery(id+"F3.opExtrude","CAP_EDGE",EDGE,{"disambiguationData":[OSD([sQuery(id+"F2.wireOp",EDGE,"E13.1.0")])],"isStart":true});
            var Q79;
            {var subQ0=sQuery(id+"F2.wireOp",EDGE,"E0");Q79=makeQuery(id+"F3.opExtrude","CAP_EDGE",EDGE,{"disambiguationData":[OSD([subQ0]),TDD([makeQuery(id+"F2.imprint","IMPRINT",EDGE,{"disambiguationData":[TD([[makeQuery(id+"F2.imprint","INTERSECT",VERTEX,{"derivedFrom":[subQ0,sQuery(id+"F2.wireOp",EDGE,"E11.MirrorCS")]}),-1.0]])],"derivedFrom":subQ0})])],"isStart":true});}
            var Q80;
            Q80=makeQuery(id+"F3.opExtrude","CAP_EDGE",EDGE,{"disambiguationData":[OSD([sQuery(id+"F2.wireOp",EDGE,"E11.MirrorCS")])],"isStart":true});
            var Q81;
            Q81=makeQuery(id+"F3.opExtrude","CAP_EDGE",EDGE,{"disambiguationData":[OSD([sQuery(id+"F2.wireOp",EDGE,"E10.trimOffspring")])],"isStart":true});
            var Q82;
            {var subQ0=sQuery(id+"F2.wireOp",EDGE,"E0");Q82=makeQuery(id+"F3.opExtrude","CAP_EDGE",EDGE,{"disambiguationData":[OSD([subQ0]),TDD([makeQuery(id+"F2.imprint","IMPRINT",EDGE,{"disambiguationData":[TD([[makeQuery(id+"F2.imprint","INTERSECT",VERTEX,{"derivedFrom":[subQ0,sQuery(id+"F2.wireOp",EDGE,"E10.trimOffspring")]}),1.0]])],"derivedFrom":subQ0})])],"isStart":true});}
            var Q83;
            Q83=makeQuery(id+"F3.opExtrude","CAP_EDGE",EDGE,{"disambiguationData":[OSD([sQuery(id+"F2.wireOp",EDGE,"E13.19.2")])],"isStart":true});
            var Q84;
            Q84=makeQuery(id+"F3.opExtrude","CAP_EDGE",EDGE,{"disambiguationData":[OSD([sQuery(id+"F2.wireOp",EDGE,"E13.19.0")])],"isStart":true});
            var Q85;
            {var subQ0=sQuery(id+"F2.wireOp",EDGE,"E0");Q85=makeQuery(id+"F3.opExtrude","CAP_EDGE",EDGE,{"disambiguationData":[OSD([subQ0]),TDD([makeQuery(id+"F2.imprint","IMPRINT",EDGE,{"disambiguationData":[TD([[makeQuery(id+"F2.imprint","INTERSECT",VERTEX,{"derivedFrom":[subQ0,sQuery(id+"F2.wireOp",EDGE,"E13.18.2")]}),-1.0]])],"derivedFrom":subQ0})])],"isStart":true});}
            var Q86;
            Q86=makeQuery(id+"F3.opExtrude","CAP_EDGE",EDGE,{"disambiguationData":[OSD([sQuery(id+"F2.wireOp",EDGE,"E13.18.2")])],"isStart":true});
            var Q87;
            Q87=makeQuery(id+"F3.opExtrude","CAP_EDGE",EDGE,{"disambiguationData":[OSD([sQuery(id+"F2.wireOp",EDGE,"E13.18.0")])],"isStart":true});
            var Q88;
            {var subQ0=sQuery(id+"F2.wireOp",EDGE,"E0");Q88=makeQuery(id+"F3.opExtrude","CAP_EDGE",EDGE,{"disambiguationData":[OSD([subQ0]),TDD([makeQuery(id+"F2.imprint","IMPRINT",EDGE,{"disambiguationData":[TD([[makeQuery(id+"F2.imprint","INTERSECT",VERTEX,{"derivedFrom":[subQ0,sQuery(id+"F2.wireOp",EDGE,"E13.17.2")]}),-1.0]])],"derivedFrom":subQ0})])],"isStart":true});}
            var Q89;
            Q89=makeQuery(id+"F3.opExtrude","CAP_EDGE",EDGE,{"disambiguationData":[OSD([sQuery(id+"F2.wireOp",EDGE,"E13.17.2")])],"isStart":true});
            var Q90;
            Q90=makeQuery(id+"F3.opExtrude","CAP_EDGE",EDGE,{"disambiguationData":[OSD([sQuery(id+"F2.wireOp",EDGE,"E13.17.0")])],"isStart":true});
            var Q91;
            {var subQ0=sQuery(id+"F2.wireOp",EDGE,"E0");Q91=makeQuery(id+"F3.opExtrude","CAP_EDGE",EDGE,{"disambiguationData":[OSD([subQ0]),TDD([makeQuery(id+"F2.imprint","IMPRINT",EDGE,{"disambiguationData":[TD([[makeQuery(id+"F2.imprint","INTERSECT",VERTEX,{"derivedFrom":[subQ0,sQuery(id+"F2.wireOp",EDGE,"E13.16.2")]}),-1.0]])],"derivedFrom":subQ0})])],"isStart":true});}
            var Q92;
            Q92=makeQuery(id+"F3.opExtrude","CAP_EDGE",EDGE,{"disambiguationData":[OSD([sQuery(id+"F2.wireOp",EDGE,"E13.16.2")])],"isStart":true});
            var Q93;
            Q93=makeQuery(id+"F3.opExtrude","CAP_EDGE",EDGE,{"disambiguationData":[OSD([sQuery(id+"F2.wireOp",EDGE,"E13.16.0")])],"isStart":true});
            var Q94;
            {var subQ0=sQuery(id+"F2.wireOp",EDGE,"E0");Q94=makeQuery(id+"F3.opExtrude","CAP_EDGE",EDGE,{"disambiguationData":[OSD([subQ0]),TDD([makeQuery(id+"F2.imprint","IMPRINT",EDGE,{"disambiguationData":[TD([[makeQuery(id+"F2.imprint","INTERSECT",VERTEX,{"derivedFrom":[subQ0,sQuery(id+"F2.wireOp",EDGE,"E13.15.2")]}),-1.0]])],"derivedFrom":subQ0})])],"isStart":true});}
            var Q95;
            Q95=makeQuery(id+"F3.opExtrude","CAP_EDGE",EDGE,{"disambiguationData":[OSD([sQuery(id+"F2.wireOp",EDGE,"E13.15.2")])],"isStart":true});
            var Q96;
            Q96=makeQuery(id+"F3.opExtrude","CAP_EDGE",EDGE,{"disambiguationData":[OSD([sQuery(id+"F2.wireOp",EDGE,"E13.15.0")])],"isStart":true});
            var Q97;
            {var subQ0=sQuery(id+"F2.wireOp",EDGE,"E0");Q97=makeQuery(id+"F3.opExtrude","CAP_EDGE",EDGE,{"disambiguationData":[OSD([subQ0]),TDD([makeQuery(id+"F2.imprint","IMPRINT",EDGE,{"disambiguationData":[TD([[makeQuery(id+"F2.imprint","INTERSECT",VERTEX,{"derivedFrom":[subQ0,sQuery(id+"F2.wireOp",EDGE,"E13.14.2")]}),-1.0]])],"derivedFrom":subQ0})])],"isStart":true});}
            var Q98;
            Q98=makeQuery(id+"F3.opExtrude","CAP_EDGE",EDGE,{"disambiguationData":[OSD([sQuery(id+"F2.wireOp",EDGE,"E13.14.2")])],"isStart":true});
            var Q99;
            Q99=makeQuery(id+"F3.opExtrude","CAP_EDGE",EDGE,{"disambiguationData":[OSD([sQuery(id+"F2.wireOp",EDGE,"E13.14.0")])],"isStart":true});
            var Q100;
            {var subQ0=sQuery(id+"F2.wireOp",EDGE,"E0");Q100=makeQuery(id+"F3.opExtrude","CAP_EDGE",EDGE,{"disambiguationData":[OSD([subQ0]),TDD([makeQuery(id+"F2.imprint","IMPRINT",EDGE,{"disambiguationData":[TD([[makeQuery(id+"F2.imprint","INTERSECT",VERTEX,{"derivedFrom":[subQ0,sQuery(id+"F2.wireOp",EDGE,"E13.13.2")]}),-1.0]])],"derivedFrom":subQ0})])],"isStart":true});}
            var Q101;
            Q101=makeQuery(id+"F3.opExtrude","CAP_EDGE",EDGE,{"disambiguationData":[OSD([sQuery(id+"F2.wireOp",EDGE,"E13.13.2")])],"isStart":true});
            var Q102;
            Q102=makeQuery(id+"F3.opExtrude","CAP_EDGE",EDGE,{"disambiguationData":[OSD([sQuery(id+"F2.wireOp",EDGE,"E13.13.0")])],"isStart":true});
            var Q103;
            {var subQ0=sQuery(id+"F2.wireOp",EDGE,"E0");Q103=makeQuery(id+"F3.opExtrude","CAP_EDGE",EDGE,{"disambiguationData":[OSD([subQ0]),TDD([makeQuery(id+"F2.imprint","IMPRINT",EDGE,{"disambiguationData":[TD([[makeQuery(id+"F2.imprint","INTERSECT",VERTEX,{"derivedFrom":[subQ0,sQuery(id+"F2.wireOp",EDGE,"E13.12.2")]}),-1.0]])],"derivedFrom":subQ0})])],"isStart":true});}
            var Q104;
            Q104=makeQuery(id+"F3.opExtrude","CAP_EDGE",EDGE,{"disambiguationData":[OSD([sQuery(id+"F2.wireOp",EDGE,"E13.12.2")])],"isStart":true});
            var Q105;
            Q105=makeQuery(id+"F3.opExtrude","CAP_EDGE",EDGE,{"disambiguationData":[OSD([sQuery(id+"F2.wireOp",EDGE,"E13.12.0")])],"isStart":true});
            var Q106;
            {var subQ0=sQuery(id+"F2.wireOp",EDGE,"E0");Q106=makeQuery(id+"F3.opExtrude","CAP_EDGE",EDGE,{"disambiguationData":[OSD([subQ0]),TDD([makeQuery(id+"F2.imprint","IMPRINT",EDGE,{"disambiguationData":[TD([[makeQuery(id+"F2.imprint","INTERSECT",VERTEX,{"derivedFrom":[subQ0,sQuery(id+"F2.wireOp",EDGE,"E13.11.2")]}),-1.0]])],"derivedFrom":subQ0})])],"isStart":true});}
            var Q107;
            Q107=makeQuery(id+"F3.opExtrude","CAP_EDGE",EDGE,{"disambiguationData":[OSD([sQuery(id+"F2.wireOp",EDGE,"E13.11.2")])],"isStart":true});
            var Q108;
            Q108=makeQuery(id+"F3.opExtrude","CAP_EDGE",EDGE,{"disambiguationData":[OSD([sQuery(id+"F2.wireOp",EDGE,"E13.11.0")])],"isStart":true});
            var Q109;
            {var subQ0=sQuery(id+"F2.wireOp",EDGE,"E0");Q109=makeQuery(id+"F3.opExtrude","CAP_EDGE",EDGE,{"disambiguationData":[OSD([subQ0]),TDD([makeQuery(id+"F2.imprint","IMPRINT",EDGE,{"disambiguationData":[TD([[makeQuery(id+"F2.imprint","INTERSECT",VERTEX,{"derivedFrom":[subQ0,sQuery(id+"F2.wireOp",EDGE,"E13.10.2")]}),-1.0]])],"derivedFrom":subQ0})])],"isStart":true});}
            var Q110;
            Q110=makeQuery(id+"F3.opExtrude","CAP_EDGE",EDGE,{"disambiguationData":[OSD([sQuery(id+"F2.wireOp",EDGE,"E13.10.2")])],"isStart":true});
            var Q111;
            Q111=makeQuery(id+"F3.opExtrude","CAP_EDGE",EDGE,{"disambiguationData":[OSD([sQuery(id+"F2.wireOp",EDGE,"E13.10.0")])],"isStart":true});
            var Q112;
            {var subQ0=sQuery(id+"F2.wireOp",EDGE,"E0");Q112=makeQuery(id+"F3.opExtrude","CAP_EDGE",EDGE,{"disambiguationData":[OSD([subQ0]),TDD([makeQuery(id+"F2.imprint","IMPRINT",EDGE,{"disambiguationData":[TD([[makeQuery(id+"F2.imprint","INTERSECT",VERTEX,{"derivedFrom":[subQ0,sQuery(id+"F2.wireOp",EDGE,"E13.9.2")]}),-1.0]])],"derivedFrom":subQ0})])],"isStart":true});}
            var Q113;
            Q113=makeQuery(id+"F3.opExtrude","CAP_EDGE",EDGE,{"disambiguationData":[OSD([sQuery(id+"F2.wireOp",EDGE,"E13.9.2")])],"isStart":true});
            var Q114;
            Q114=makeQuery(id+"F3.opExtrude","CAP_EDGE",EDGE,{"disambiguationData":[OSD([sQuery(id+"F2.wireOp",EDGE,"E13.9.0")])],"isStart":true});
            var Q115;
            {var subQ0=sQuery(id+"F2.wireOp",EDGE,"E0");Q115=makeQuery(id+"F3.opExtrude","CAP_EDGE",EDGE,{"disambiguationData":[OSD([subQ0]),TDD([makeQuery(id+"F2.imprint","IMPRINT",EDGE,{"disambiguationData":[TD([[makeQuery(id+"F2.imprint","INTERSECT",VERTEX,{"derivedFrom":[subQ0,sQuery(id+"F2.wireOp",EDGE,"E13.8.2")]}),-1.0]])],"derivedFrom":subQ0})])],"isStart":true});}
            var Q116;
            Q116=makeQuery(id+"F3.opExtrude","CAP_EDGE",EDGE,{"disambiguationData":[OSD([sQuery(id+"F2.wireOp",EDGE,"E13.8.2")])],"isStart":true});
            fillet(context, id + "F4", {"entities" : qUnion([Q0, Q1, Q2, Q3, Q4, Q5, Q6, Q7, Q8, Q9, Q10, Q11, Q12, Q13, Q14, Q15, Q16, Q17, Q18, Q19, Q20, Q21, Q22, Q23, Q24, Q25, Q26, Q27, Q28, Q29, Q30, Q31, Q32, Q33, Q34, Q35, Q36, Q37, Q38, Q39, Q40, Q41, Q42, Q43, Q44, Q45, Q46, Q47, Q48, Q49, Q50, Q51, Q52, Q53, Q54, Q55, Q56, Q57, Q58, Q59, Q60, Q61, Q62, Q63, Q64, Q65, Q66, Q67, Q68, Q69, Q70, Q71, Q72, Q73, Q74, Q75, Q76, Q77, Q78, Q79, Q80, Q81, Q82, Q83, Q84, Q85, Q86, Q87, Q88, Q89, Q90, Q91, Q92, Q93, Q94, Q95, Q96, Q97, Q98, Q99, Q100, Q101, Q102, Q103, Q104, Q105, Q106, Q107, Q108, Q109, Q110, Q111, Q112, Q113, Q114, Q115, Q116]), "radius" : (getVariable(context, 'TeethFillet')) * mm, "tangentPropagation" : true, "allowEdgeOverflow" : false});
        }
        {
            var Q0;
            Q0=makeQuery(id+"F3.opExtrude","CAP_FACE",FACE,{"disambiguationData":[OSD([sQuery(id+"F2.wireOp",EDGE,"E0"),sQuery(id+"F2.wireOp",EDGE,"E10.trimOffspring"),sQuery(id+"F2.wireOp",EDGE,"E11.MirrorCS"),sQuery(id+"F2.wireOp",EDGE,"E12"),sQuery(id+"F2.wireOp",EDGE,"E13.1.0"),sQuery(id+"F2.wireOp",EDGE,"E13.1.1"),sQuery(id+"F2.wireOp",EDGE,"E13.1.2"),sQuery(id+"F2.wireOp",EDGE,"E13.2.0"),sQuery(id+"F2.wireOp",EDGE,"E13.2.1"),sQuery(id+"F2.wireOp",EDGE,"E13.2.2"),sQuery(id+"F2.wireOp",EDGE,"E13.3.0"),sQuery(id+"F2.wireOp",EDGE,"E13.3.1"),sQuery(id+"F2.wireOp",EDGE,"E13.3.2"),sQuery(id+"F2.wireOp",EDGE,"E13.4.0"),sQuery(id+"F2.wireOp",EDGE,"E13.4.1"),sQuery(id+"F2.wireOp",EDGE,"E13.4.2"),sQuery(id+"F2.wireOp",EDGE,"E13.5.0"),sQuery(id+"F2.wireOp",EDGE,"E13.5.1"),sQuery(id+"F2.wireOp",EDGE,"E13.5.2"),sQuery(id+"F2.wireOp",EDGE,"E13.6.0"),sQuery(id+"F2.wireOp",EDGE,"E13.6.1"),sQuery(id+"F2.wireOp",EDGE,"E13.6.2"),sQuery(id+"F2.wireOp",EDGE,"E13.7.0"),sQuery(id+"F2.wireOp",EDGE,"E13.7.1"),sQuery(id+"F2.wireOp",EDGE,"E13.7.2"),sQuery(id+"F2.wireOp",EDGE,"E13.8.0"),sQuery(id+"F2.wireOp",EDGE,"E13.8.1"),sQuery(id+"F2.wireOp",EDGE,"E13.8.2"),sQuery(id+"F2.wireOp",EDGE,"E13.9.0"),sQuery(id+"F2.wireOp",EDGE,"E13.9.1"),sQuery(id+"F2.wireOp",EDGE,"E13.9.2"),sQuery(id+"F2.wireOp",EDGE,"E13.10.0"),sQuery(id+"F2.wireOp",EDGE,"E13.10.1"),sQuery(id+"F2.wireOp",EDGE,"E13.10.2"),sQuery(id+"F2.wireOp",EDGE,"E13.11.0"),sQuery(id+"F2.wireOp",EDGE,"E13.11.1"),sQuery(id+"F2.wireOp",EDGE,"E13.11.2"),sQuery(id+"F2.wireOp",EDGE,"E13.12.0"),sQuery(id+"F2.wireOp",EDGE,"E13.12.1"),sQuery(id+"F2.wireOp",EDGE,"E13.12.2"),sQuery(id+"F2.wireOp",EDGE,"E13.13.0"),sQuery(id+"F2.wireOp",EDGE,"E13.13.1"),sQuery(id+"F2.wireOp",EDGE,"E13.13.2"),sQuery(id+"F2.wireOp",EDGE,"E13.14.0"),sQuery(id+"F2.wireOp",EDGE,"E13.14.1"),sQuery(id+"F2.wireOp",EDGE,"E13.14.2"),sQuery(id+"F2.wireOp",EDGE,"E13.15.0"),sQuery(id+"F2.wireOp",EDGE,"E13.15.1"),sQuery(id+"F2.wireOp",EDGE,"E13.15.2"),sQuery(id+"F2.wireOp",EDGE,"E13.16.0"),sQuery(id+"F2.wireOp",EDGE,"E13.16.1"),sQuery(id+"F2.wireOp",EDGE,"E13.16.2"),sQuery(id+"F2.wireOp",EDGE,"E13.17.0"),sQuery(id+"F2.wireOp",EDGE,"E13.17.1"),sQuery(id+"F2.wireOp",EDGE,"E13.17.2"),sQuery(id+"F2.wireOp",EDGE,"E13.18.0"),sQuery(id+"F2.wireOp",EDGE,"E13.18.1"),sQuery(id+"F2.wireOp",EDGE,"E13.18.2"),sQuery(id+"F2.wireOp",EDGE,"E13.19.0"),sQuery(id+"F2.wireOp",EDGE,"E13.19.1"),sQuery(id+"F2.wireOp",EDGE,"E13.19.2"),sQuery(id+"F2.wireOp",EDGE,"E14")])],"isStart":false});
            var sketch = newSketch(context, id + "F5", { "sketchPlane" : qUnion([Q0])});
            skCircle(sketch, "E15", {"center": v(0, 0) * mm, "radius": 7.3 * mm});
            skSolve(sketch);
        }
        {
            var Q0;
            Q0=makeQuery(id+"F5.imprint","IMPRINT",FACE,{"disambiguationData":[TD([[makeQuery(id+"F5.imprint","IMPRINT",EDGE,{"derivedFrom":sQuery(id+"F5.wireOp",EDGE,"E15")}),1.0]])]});
            extrude(context, id + "F6", {"entities" : qUnion([Q0]), "operationType" : NewBodyOperationType.REMOVE, "oppositeDirection" : true, "depth" : 5 * mm, "offsetDistance" : 25 * mm});
        }
    });
